# Revit family: result
name_source: partatom
category: Mechanical Equipment
units: mm (PartAtom-declared; Revit-internal decimal feet)

## family parameters
Always vertical = No
Classification = None
Cut with Voids When Loaded = No
Maintain Annotation Orientation = No
OmniClass Number = 23.75.70.14.34
OmniClass Title = Air Duct Accessories
Part Type = Normal
Room Calculation Point = No
Round Connector Dimension = Use Diameter
Shared = No
Work Plane-Based = Yes

## types (1)
- -1-NASHIRA S 150 R8  - Heat Recovery Units
    Autor = BIM6D
    Aux.1 = 5 mm  [stored 0.0164042 ft]
    Aux.2 = 150 mm
    Aux.3 = 170 mm  [stored 0.557743 ft]
    Aux.4 = 120 mm  [stored 0.393701 ft]
    CorrienteNominal = 0 A
    Default Elevation = 1219 mm
    Description = Enthalpy Recovery Unit up to 150 m3/h.Featuring 86% thermal efficiency according to eco-design standard. With low consumption, low-noise EC motors (23W at reference airflow) it ensures a energy-efficient environment. The Unit is Passivhaus certificated and builds in constant airflow motors that can work in combination with the internal RH sensors in order to maintain a comfortable and healthy indoor climate.NASHIRA is reversible and symmetrical with 90º adjustable nozzles for an easier installation. Includes wired remote (manual/auto control and alarm messages)4 outlets ø125mm.&nbsp;
    Diametro Conector 1 = 125 mm  [stored 0.410105 ft]
    FlujoAire1 = 0.0 L/s
    FlujoAire2 = 0.0 L/s
    FlujoAire3 = 0.0 L/s
    FlujoAire4 = 0.0 L/s
    IfcExportAs = IfcAirTerminalBoxType
    IfcExportType = CONSTANTFLOW
    IndiceFlujoNominal = 0.0 L/s
    IndicePotenciaNominal = 0 W
    Manufacturer = S&P Sistemas de Ventilación S.L.U.
    MasterformatCodigo = 23 36 00
    MasterformatTitulo = Air Terminal Units
    Material Carcasa = SP_Plastic_Grey
    Material Carcasa B = SP_Plastic_White
    Material Conector Bornes = SP_Plastic_Red
    Model = NASHIRA
    OmniclassCodigo = 23.75.70.21.31
    OmniclassTitulo = Exhaust Terminals
    PA = 1000 mm  [stored 3.28084 ft]
    PB = 600 mm  [stored 1.9685 ft]
    PC = 210 mm  [stored 0.688976 ft]
    PD = 125 mm  [stored 0.410105 ft]
    PE = 1024 mm  [stored 3.35958 ft]
    PEXH_AIR = 0.00°
    PEXT_AIR = 0.00°
    PF = 575 mm
    PG = 300 mm
    PH = 114 mm  [stored 0.374016 ft]
    PII = 0 mm  [stored 0 ft]
    PJ = 22 mm  [stored 0.0721785 ft]
    POUT_AIR = 0.00°
    PSUP_AIR = 0.00°
    PesoBruto = 0.00 kg
    PresionDinamica = 0.0 Pa
    PresionEstaticaNominal = 0.0 Pa
    PresionTotalNominal = 0.0 Pa
    TensionNominal = 0 V
    Type Image = <None>
    UNSPSCCodigo = 72151204
    UNSPSCTitulo = HVAC ventilation and duct work construction service
    URL = https://www.solerpalau.com
    Uniclass2.0Codigo = 23.75.70.14.34
    Uniclass2.0Titulo = Ductwork accessories
    spIntensidadMaximaAbsorbida = 0 A
    spPotenciaElectrica_Solucion = 0 W
    spPotenciaUtil_Solucion = 0 W
    spTamañoVentilador = 0 mm  [stored 0 ft]
    sp_Montaje = 1

note: [stored X ft] marks values corroborated as IEEE doubles in the binary element streams (Revit-internal decimal feet)
